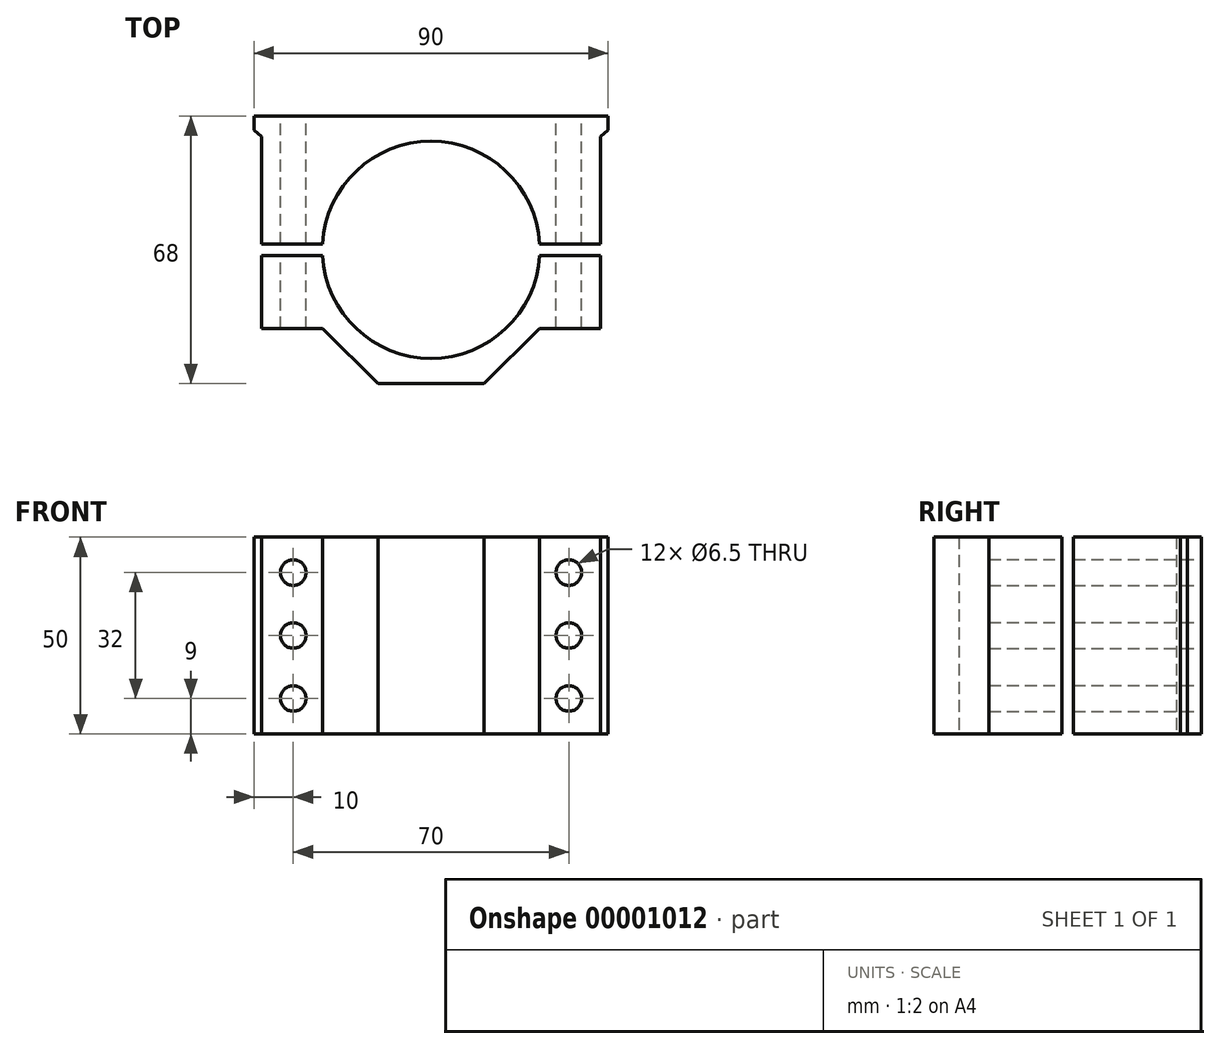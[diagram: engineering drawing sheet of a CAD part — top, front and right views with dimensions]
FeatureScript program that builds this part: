
annotation { "Feature Type Name" : "Feature", "Feature Type Description" : "" }
export const myFeature = defineFeature(function(context is Context, id is Id, definition is map)
    precondition{}
    {
        {
            var Q0;
            Q0=qCreatedBy(makeId("Front.planeOp"),FACE);
            var sketch = newSketch(context, id + "F0", { "sketchPlane" : qUnion([Q0])});
            skLineSegment(sketch, "E0.rect.bottom", {"start": v(-45, -25) * mm, "end": v(45, -25) * mm});
            skLineSegment(sketch, "E0.rect.top", {"start": v(-45, 25) * mm, "end": v(45, 25) * mm});
            skLineSegment(sketch, "E0.rect.left", {"start": v(-45, -25) * mm, "end": v(-45, 25) * mm});
            skLineSegment(sketch, "E0.rect.right", {"start": v(45, -25) * mm, "end": v(45, 25) * mm});
            skPoint(sketch, "E0.rect.middle", {"position": v(0, 0) * mm});
            skCircle(sketch, "E1", {"center": v(35, 0) * mm, "radius": 3.25 * mm});
            skCircle(sketch, "E2", {"center": v(35, -16) * mm, "radius": 3.25 * mm});
            skCircle(sketch, "E3", {"center": v(35, 16) * mm, "radius": 3.25 * mm});
            skCircle(sketch, "E4", {"center": v(-35, 0) * mm, "radius": 3.25 * mm});
            skCircle(sketch, "E5", {"center": v(-35, -16) * mm, "radius": 3.25 * mm});
            skCircle(sketch, "E6", {"center": v(-35, 16) * mm, "radius": 3.25 * mm});
            skSolve(sketch);
        }
        {
            var Q0;
            Q0=makeQuery(id+"F0.imprint","IMPRINT",FACE,{"disambiguationData":[TD([[makeQuery(id+"F0.imprint","IMPRINT",EDGE,{"derivedFrom":sQuery(id+"F0.wireOp",EDGE,"E0.rect.bottom")}),1.0]])]});
            extrude(context, id + "F1", {"entities" : qUnion([Q0]), "endBound" : BoundingType.SYMMETRIC, "depth" : 68 * mm});
        }
        {
            var Q0;
            Q0=makeQuery(id+"F1.opExtrude","SWEPT_FACE",FACE,{"disambiguationData":[OSD([sQuery(id+"F0.wireOp",EDGE,"E0.rect.bottom")])]});
            var sketch = newSketch(context, id + "F2", { "sketchPlane" : qUnion([Q0])});
            skCircle(sketch, "E7", {"center": v(0, 0) * mm, "radius": 27.6 * mm});
            skLineSegment(sketch, "E8", {"start": v(43, -28.7) * mm, "end": v(43, 20) * mm});
            skLineSegment(sketch, "E9.0.MirrorCS", {"start": v(-43, -28.7) * mm, "end": v(-43, 20) * mm, "construction": true});
            skLineSegment(sketch, "E10", {"start": v(43, 20) * mm, "end": v(27.5, 20) * mm});
            skLineSegment(sketch, "E11", {"start": v(45, -30.4) * mm, "end": v(43, -28.7) * mm});
            skLineSegment(sketch, "E12", {"start": v(27.5, 20) * mm, "end": v(13.5, 34) * mm});
            skLineSegment(sketch, "E13.0.MirrorCS", {"start": v(-43, -28.7) * mm, "end": v(-43, 20) * mm});
            skLineSegment(sketch, "E14.0.MirrorCS", {"start": v(-45, -30.4) * mm, "end": v(-43, -28.7) * mm});
            skLineSegment(sketch, "E15.0.MirrorCS", {"start": v(-27.5, 20) * mm, "end": v(-13.5, 34) * mm});
            skLineSegment(sketch, "E16.trimOffspring", {"start": v(-27.5, 20) * mm, "end": v(-43, 20) * mm});
            skLineSegment(sketch, "E17", {"start": v(-45, -30.4) * mm, "end": v(-45, 34) * mm});
            skLineSegment(sketch, "E18", {"start": v(-45, 34) * mm, "end": v(-13.5, 34) * mm});
            skLineSegment(sketch, "E19", {"start": v(13.5, 34) * mm, "end": v(45, 34) * mm});
            skLineSegment(sketch, "E20", {"start": v(45, 34) * mm, "end": v(45, -30.4) * mm});
            skPoint(sketch, "E21.0.MirrorCS.start.orphan", {"position": v(-45, -34) * mm});
            skPoint(sketch, "E22.0.MirrorCS.start.orphan", {"position": v(0, -34) * mm});
            skPoint(sketch, "E23.start.orphan", {"position": v(45, -34) * mm});
            skPoint(sketch, "E24.orphan", {"position": v(-27.5, 51.68) * mm});
            skPoint(sketch, "E25.0.MirrorCS.start.orphan", {"position": v(-13.5, 50.21) * mm});
            skPoint(sketch, "E26.start.orphan", {"position": v(13.5, 50.21) * mm});
            skPoint(sketch, "E27.orphan", {"position": v(27.5, 51.68) * mm});
            skPoint(sketch, "E28.0.MirrorCS.end.orphan", {"position": v(-27.5, 20.58) * mm});
            skPoint(sketch, "E29.trimOffspring.end.orphan", {"position": v(-43, 41.37) * mm});
            skPoint(sketch, "E30.0.MirrorCS.start.orphan", {"position": v(0, 34) * mm});
            skPoint(sketch, "E31.orphan", {"position": v(43, -34) * mm});
            skPoint(sketch, "E32.orphan", {"position": v(-43, -34) * mm});
            skPoint(sketch, "E33.start.orphan", {"position": v(0, -40.2) * mm});
            skSolve(sketch);
        }
        {
            var Q0;
            Q0=makeQuery(id+"F2.imprint","IMPRINT",FACE,{"disambiguationData":[TD([[makeQuery(id+"F2.imprint","IMPRINT",EDGE,{"derivedFrom":sQuery(id+"F2.wireOp",EDGE,"E7")}),1.0]])]});
            var Q1;
            Q1=makeQuery(id+"F2.imprint","IMPRINT",FACE,{"disambiguationData":[TD([[makeQuery(id+"F2.imprint","IMPRINT",EDGE,{"derivedFrom":sQuery(id+"F2.wireOp",EDGE,"E13.0.MirrorCS")}),1.0]])]});
            var Q2;
            Q2=makeQuery(id+"F2.imprint","IMPRINT",FACE,{"disambiguationData":[TD([[makeQuery(id+"F2.imprint","IMPRINT",EDGE,{"derivedFrom":sQuery(id+"F2.wireOp",EDGE,"E11")}),-1.0]])]});
            extrude(context, id + "F3", {"entities" : qUnion([Q0, Q1, Q2]), "operationType" : NewBodyOperationType.REMOVE, "endBound" : BoundingType.THROUGH_ALL, "oppositeDirection" : true, "depth" : 25.4 * mm});
        }
        {
            var Q0;
            Q0=makeQuery(id+"F1.opExtrude","SWEPT_FACE",FACE,{"disambiguationData":[OSD([sQuery(id+"F0.wireOp",EDGE,"E0.rect.bottom")])]});
            var sketch = newSketch(context, id + "F4", { "sketchPlane" : qUnion([Q0])});
            skLineSegment(sketch, "E34.rect.bottom", {"start": v(47.5, -1.5) * mm, "end": v(-47.5, -1.5) * mm});
            skLineSegment(sketch, "E34.rect.top", {"start": v(47.5, 1.5) * mm, "end": v(-47.5, 1.5) * mm});
            skLineSegment(sketch, "E34.rect.left", {"start": v(47.5, -1.5) * mm, "end": v(47.5, 1.5) * mm});
            skLineSegment(sketch, "E34.rect.right", {"start": v(-47.5, -1.5) * mm, "end": v(-47.5, 1.5) * mm});
            skPoint(sketch, "E34.rect.middle", {"position": v(0, 0) * mm});
            skSolve(sketch);
        }
        {
            var Q0;
            {var subQ0=makeQuery(id+"F3.boolean.opBoolean","COPY",EDGE,{"derivedFrom":makeQuery(id+"F3.opExtrude","CAP_EDGE",EDGE,{"disambiguationData":[OSD([sQuery(id+"F2.wireOp",EDGE,"E8")])],"isStart":true})});var subQ3=sQuery(id+"F4.wireOp",EDGE,"E34.rect.bottom");var subQ4=makeQuery(id+"F4.imprint","INTERSECT",VERTEX,{"derivedFrom":[subQ0,subQ3]});var subQ6=sQuery(id+"F4.wireOp",EDGE,"E34.rect.left");var subQ7=makeQuery(id+"F3.boolean.opBoolean","COPY",EDGE,{"derivedFrom":makeQuery(id+"F3.opExtrude","CAP_EDGE",EDGE,{"disambiguationData":[OSD([sQuery(id+"F2.wireOp",EDGE,"E13.0.MirrorCS")])],"isStart":true})});var subQ9=makeQuery(id+"F4.imprint","INTERSECT",VERTEX,{"derivedFrom":[subQ7,subQ3]});var subQ11=sQuery(id+"F4.wireOp",EDGE,"E34.rect.right");var subQ12=makeQuery(id+"F3.boolean.opBoolean","COPY",EDGE,{"derivedFrom":makeQuery(id+"F3.opExtrude","CAP_EDGE",EDGE,{"disambiguationData":[OSD([sQuery(id+"F2.wireOp",EDGE,"E7")])],"isStart":true})});var subQ14=makeQuery(id+"F4.imprint","INTERSECT",VERTEX,{"disambiguationData":[OD(0.0)],"derivedFrom":[subQ12,subQ3]});Q0=qUnion([makeQuery(id+"F4.imprint","IMPRINT",FACE,{"disambiguationData":[TD([[makeQuery(id+"F4.imprint","IMPRINT",EDGE,{"derivedFrom":subQ6}),1.0]])]}),makeQuery(id+"F4.imprint","IMPRINT",FACE,{"disambiguationData":[TD([[makeQuery(id+"F4.imprint","IMPRINT",EDGE,{"derivedFrom":subQ11}),-1.0]])]}),makeQuery(id+"F4.imprint","IMPRINT",FACE,{"disambiguationData":[TD([[makeQuery(id+"F4.imprint","IMPRINT",EDGE,{"disambiguationData":[TD([[subQ4,-1.0]])],"derivedFrom":subQ3}),-1.0]])]}),makeQuery(id+"F4.imprint","IMPRINT",FACE,{"disambiguationData":[TD([[makeQuery(id+"F4.imprint","IMPRINT",EDGE,{"disambiguationData":[TD([[subQ14,-1.0]])],"derivedFrom":subQ3}),-1.0]])]}),makeQuery(id+"F4.imprint","IMPRINT",FACE,{"disambiguationData":[TD([[makeQuery(id+"F4.imprint","IMPRINT",EDGE,{"disambiguationData":[TD([[subQ9,1.0]])],"derivedFrom":subQ3}),-1.0]])]})]);}
            extrude(context, id + "F5", {"entities" : qUnion([Q0]), "operationType" : NewBodyOperationType.REMOVE, "endBound" : BoundingType.THROUGH_ALL, "oppositeDirection" : true, "depth" : 25.4 * mm});
        }
    });
